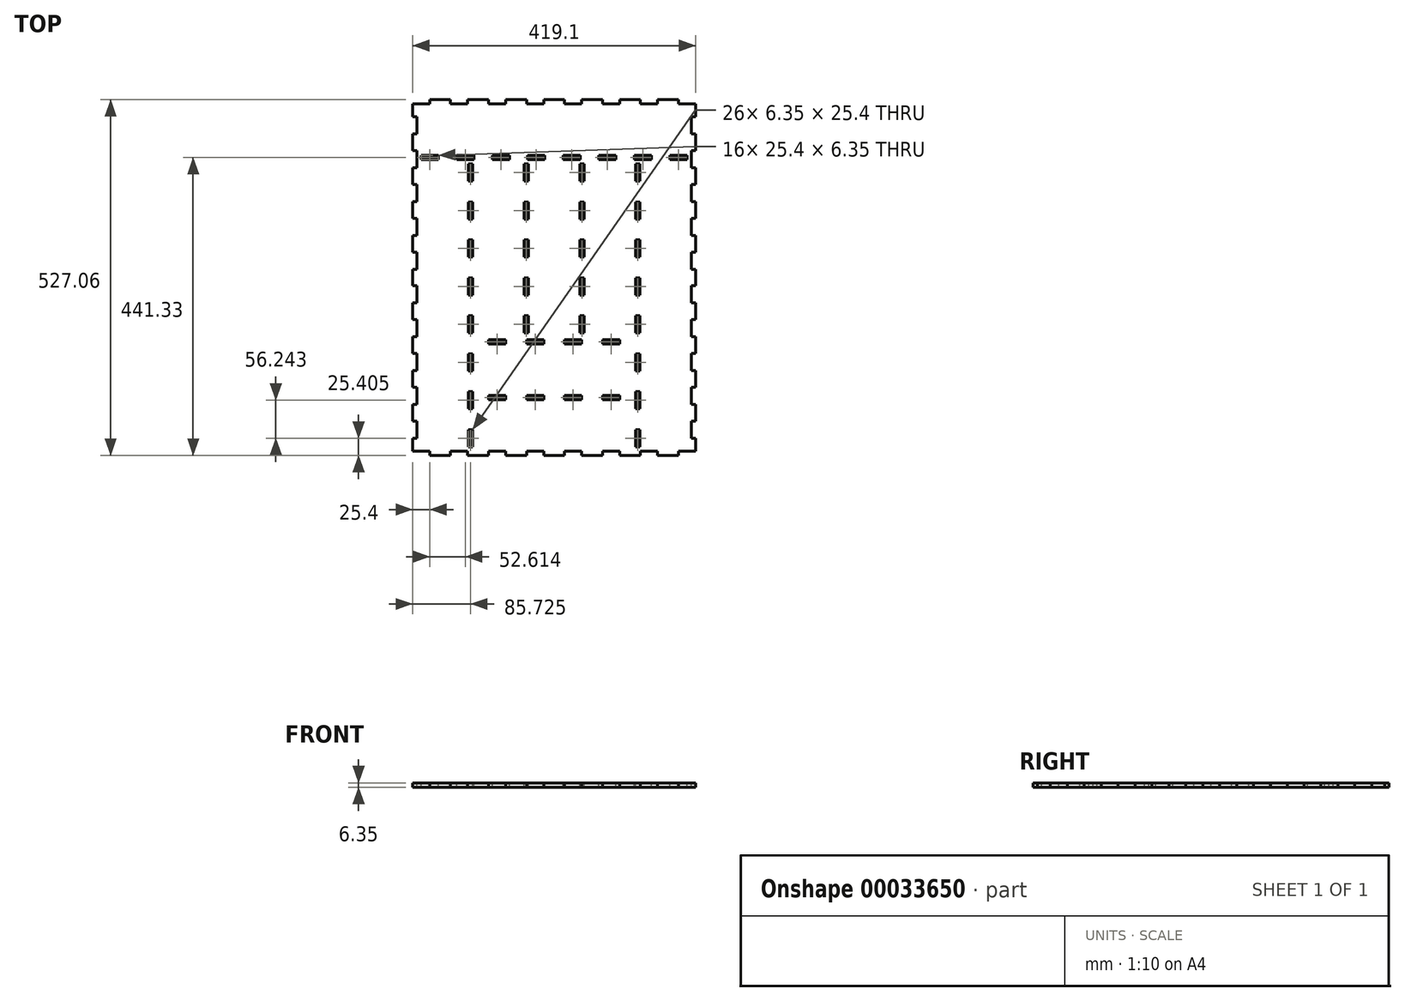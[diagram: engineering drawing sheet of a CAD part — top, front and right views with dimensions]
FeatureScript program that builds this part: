
annotation { "Feature Type Name" : "Feature", "Feature Type Description" : "" }
export const myFeature = defineFeature(function(context is Context, id is Id, definition is map)
    precondition{}
    {
        {
            var Q0;
            Q0=qCreatedBy(makeId("Top.planeOp"),FACE);
            var sketch = newSketch(context, id + "F0", { "sketchPlane" : qUnion([Q0])});
            skLineSegment(sketch, "E0.rect.bottom", {"start": v(209.55, 263.53) * mm, "end": v(-209.55, 263.53) * mm});
            skLineSegment(sketch, "E0.rect.top", {"start": v(209.55, -263.53) * mm, "end": v(-209.55, -263.53) * mm});
            skLineSegment(sketch, "E0.rect.left", {"start": v(209.55, 263.53) * mm, "end": v(209.55, -263.53) * mm});
            skLineSegment(sketch, "E0.rect.right", {"start": v(-209.55, 263.53) * mm, "end": v(-209.55, -263.53) * mm});
            skPoint(sketch, "E0.rect.middle", {"position": v(0, 0) * mm});
            skSolve(sketch);
        }
        {
            var Q0;
            Q0=makeQuery(id+"F0.imprint","IMPRINT",FACE,{"disambiguationData":[TD([[makeQuery(id+"F0.imprint","IMPRINT",EDGE,{"derivedFrom":sQuery(id+"F0.wireOp",EDGE,"E0.rect.bottom")}),1.0]])]});
            extrude(context, id + "F1", {"entities" : qUnion([Q0]), "depth" : 6.35 * mm});
        }
        {
            var Q0;
            Q0=makeQuery(id+"F1.opExtrude","CAP_FACE",FACE,{"disambiguationData":[OSD([sQuery(id+"F0.wireOp",EDGE,"E0.rect.bottom"),sQuery(id+"F0.wireOp",EDGE,"E0.rect.top"),sQuery(id+"F0.wireOp",EDGE,"E0.rect.left"),sQuery(id+"F0.wireOp",EDGE,"E0.rect.right")])],"isStart":false});
            var sketch = newSketch(context, id + "F2", { "sketchPlane" : qUnion([Q0])});
            skLineSegment(sketch, "E1.bottom", {"start": v(-209.55, -257.18) * mm, "end": v(-184.15, -257.18) * mm});
            skLineSegment(sketch, "E1.top", {"start": v(-209.55, -263.53) * mm, "end": v(-184.15, -263.53) * mm});
            skLineSegment(sketch, "E1.left", {"start": v(-209.55, -257.18) * mm, "end": v(-209.55, -263.53) * mm});
            skLineSegment(sketch, "E1.right", {"start": v(-184.15, -257.18) * mm, "end": v(-184.15, -263.53) * mm});
            skLineSegment(sketch, "E2", {"start": v(-209.55, 0) * mm, "end": v(209.55, 0) * mm, "construction": true});
            skLineSegment(sketch, "E3", {"start": v(0, 263.53) * mm, "end": v(0, -263.53) * mm, "construction": true});
            skLineSegment(sketch, "E4.1.0.0", {"start": v(-127.9, -257.18) * mm, "end": v(-127.9, -263.53) * mm});
            skLineSegment(sketch, "E4.1.0.1", {"start": v(-153.3, -257.18) * mm, "end": v(-153.3, -263.53) * mm});
            skLineSegment(sketch, "E4.1.0.2", {"start": v(-153.3, -263.53) * mm, "end": v(-127.9, -263.53) * mm});
            skLineSegment(sketch, "E4.1.0.3", {"start": v(-153.3, -257.18) * mm, "end": v(-127.9, -257.18) * mm});
            skLineSegment(sketch, "E4.2.0.0", {"start": v(-71.66, -257.18) * mm, "end": v(-71.66, -263.53) * mm});
            skLineSegment(sketch, "E4.2.0.1", {"start": v(-97.06, -257.18) * mm, "end": v(-97.06, -263.53) * mm});
            skLineSegment(sketch, "E4.2.0.2", {"start": v(-97.06, -263.53) * mm, "end": v(-71.66, -263.53) * mm});
            skLineSegment(sketch, "E4.2.0.3", {"start": v(-97.06, -257.18) * mm, "end": v(-71.66, -257.18) * mm});
            skLineSegment(sketch, "E4.3.0.0", {"start": v(-15.42, -257.18) * mm, "end": v(-15.42, -263.53) * mm});
            skLineSegment(sketch, "E4.3.0.1", {"start": v(-40.82, -257.18) * mm, "end": v(-40.82, -263.53) * mm});
            skLineSegment(sketch, "E4.3.0.2", {"start": v(-40.82, -263.53) * mm, "end": v(-15.42, -263.53) * mm});
            skLineSegment(sketch, "E4.3.0.3", {"start": v(-40.82, -257.18) * mm, "end": v(-15.42, -257.18) * mm});
            skLineSegment(sketch, "E4.4.0.0", {"start": v(40.82, -257.18) * mm, "end": v(40.82, -263.53) * mm});
            skLineSegment(sketch, "E4.4.0.1", {"start": v(15.42, -257.18) * mm, "end": v(15.42, -263.53) * mm});
            skLineSegment(sketch, "E4.4.0.2", {"start": v(15.42, -263.53) * mm, "end": v(40.82, -263.53) * mm});
            skLineSegment(sketch, "E4.4.0.3", {"start": v(15.42, -257.18) * mm, "end": v(40.82, -257.18) * mm});
            skLineSegment(sketch, "E4.5.0.0", {"start": v(97.06, -257.18) * mm, "end": v(97.06, -263.53) * mm});
            skLineSegment(sketch, "E4.5.0.1", {"start": v(71.66, -257.18) * mm, "end": v(71.66, -263.53) * mm});
            skLineSegment(sketch, "E4.5.0.2", {"start": v(71.66, -263.53) * mm, "end": v(97.06, -263.53) * mm});
            skLineSegment(sketch, "E4.5.0.3", {"start": v(71.66, -257.18) * mm, "end": v(97.06, -257.18) * mm});
            skLineSegment(sketch, "E4.6.0.0", {"start": v(153.3, -257.18) * mm, "end": v(153.3, -263.53) * mm});
            skLineSegment(sketch, "E4.6.0.1", {"start": v(127.9, -257.18) * mm, "end": v(127.9, -263.53) * mm});
            skLineSegment(sketch, "E4.6.0.2", {"start": v(127.9, -263.53) * mm, "end": v(153.3, -263.53) * mm});
            skLineSegment(sketch, "E4.6.0.3", {"start": v(127.9, -257.18) * mm, "end": v(153.3, -257.18) * mm});
            skLineSegment(sketch, "E4.7.0.0", {"start": v(209.55, -257.18) * mm, "end": v(209.55, -263.53) * mm});
            skLineSegment(sketch, "E4.7.0.1", {"start": v(184.15, -257.18) * mm, "end": v(184.15, -263.53) * mm});
            skLineSegment(sketch, "E4.7.0.2", {"start": v(184.15, -263.53) * mm, "end": v(209.55, -263.53) * mm});
            skLineSegment(sketch, "E4.7.0.3", {"start": v(184.15, -257.18) * mm, "end": v(209.55, -257.18) * mm});
            skLineSegment(sketch, "E4.direction1", {"start": v(-184.15, -263.53) * mm, "end": v(-127.9, -263.53) * mm, "construction": true});
            skLineSegment(sketch, "E5.MirrorCS", {"start": v(127.9, 257.18) * mm, "end": v(127.9, 263.53) * mm});
            skLineSegment(sketch, "E6.MirrorCS", {"start": v(15.42, 257.18) * mm, "end": v(15.42, 263.53) * mm});
            skLineSegment(sketch, "E7.MirrorCS", {"start": v(209.55, 257.18) * mm, "end": v(209.55, 263.53) * mm});
            skLineSegment(sketch, "E8.MirrorCS", {"start": v(184.15, 257.18) * mm, "end": v(184.15, 263.53) * mm});
            skLineSegment(sketch, "E9.MirrorCS", {"start": v(97.06, 257.18) * mm, "end": v(97.06, 263.53) * mm});
            skLineSegment(sketch, "E10.MirrorCS", {"start": v(71.66, 257.18) * mm, "end": v(71.66, 263.53) * mm});
            skLineSegment(sketch, "E11.MirrorCS", {"start": v(153.3, 257.18) * mm, "end": v(153.3, 263.53) * mm});
            skLineSegment(sketch, "E12.MirrorCS", {"start": v(40.82, 257.18) * mm, "end": v(40.82, 263.53) * mm});
            skLineSegment(sketch, "E13.MirrorCS", {"start": v(127.9, 257.18) * mm, "end": v(153.3, 257.18) * mm});
            skLineSegment(sketch, "E14.MirrorCS", {"start": v(15.42, 263.53) * mm, "end": v(40.82, 263.53) * mm});
            skLineSegment(sketch, "E15.MirrorCS", {"start": v(127.9, 263.53) * mm, "end": v(153.3, 263.53) * mm});
            skLineSegment(sketch, "E16.MirrorCS", {"start": v(15.42, 257.18) * mm, "end": v(40.82, 257.18) * mm});
            skLineSegment(sketch, "E17.MirrorCS", {"start": v(184.15, 263.53) * mm, "end": v(209.55, 263.53) * mm});
            skLineSegment(sketch, "E18.MirrorCS", {"start": v(71.66, 263.53) * mm, "end": v(97.06, 263.53) * mm});
            skLineSegment(sketch, "E19.MirrorCS", {"start": v(184.15, 257.18) * mm, "end": v(209.55, 257.18) * mm});
            skLineSegment(sketch, "E20.MirrorCS", {"start": v(71.66, 257.18) * mm, "end": v(97.06, 257.18) * mm});
            skLineSegment(sketch, "E21.MirrorCS", {"start": v(-127.9, 257.18) * mm, "end": v(-127.9, 263.53) * mm});
            skLineSegment(sketch, "E22.MirrorCS", {"start": v(-184.15, 257.18) * mm, "end": v(-184.15, 263.53) * mm});
            skLineSegment(sketch, "E23.MirrorCS", {"start": v(-153.3, 257.18) * mm, "end": v(-127.9, 257.18) * mm});
            skLineSegment(sketch, "E24.MirrorCS", {"start": v(-209.55, 263.53) * mm, "end": v(-184.15, 263.53) * mm});
            skLineSegment(sketch, "E25.MirrorCS", {"start": v(-40.82, 257.18) * mm, "end": v(-40.82, 263.53) * mm});
            skLineSegment(sketch, "E26.MirrorCS", {"start": v(-97.06, 263.53) * mm, "end": v(-71.66, 263.53) * mm});
            skLineSegment(sketch, "E27.MirrorCS", {"start": v(-97.06, 257.18) * mm, "end": v(-71.66, 257.18) * mm});
            skLineSegment(sketch, "E28.MirrorCS", {"start": v(-97.06, 257.18) * mm, "end": v(-97.06, 263.53) * mm});
            skLineSegment(sketch, "E29.MirrorCS", {"start": v(-71.66, 257.18) * mm, "end": v(-71.66, 263.53) * mm});
            skLineSegment(sketch, "E30.MirrorCS", {"start": v(-153.3, 263.53) * mm, "end": v(-127.9, 263.53) * mm});
            skLineSegment(sketch, "E31.MirrorCS", {"start": v(-153.3, 257.18) * mm, "end": v(-153.3, 263.53) * mm});
            skLineSegment(sketch, "E32.MirrorCS", {"start": v(-209.55, 257.18) * mm, "end": v(-209.55, 263.53) * mm});
            skLineSegment(sketch, "E33.MirrorCS", {"start": v(-209.55, 257.18) * mm, "end": v(-184.15, 257.18) * mm});
            skLineSegment(sketch, "E34.MirrorCS", {"start": v(-15.42, 257.18) * mm, "end": v(-15.42, 263.53) * mm});
            skLineSegment(sketch, "E35.MirrorCS", {"start": v(-184.15, 263.53) * mm, "end": v(-127.9, 263.53) * mm});
            skLineSegment(sketch, "E36.MirrorCS", {"start": v(-40.82, 257.18) * mm, "end": v(-15.42, 257.18) * mm});
            skLineSegment(sketch, "E37.MirrorCS", {"start": v(-40.82, 263.53) * mm, "end": v(-15.42, 263.53) * mm});
            skLineSegment(sketch, "E38.bottom", {"start": v(-209.55, 238.13) * mm, "end": v(-203.2, 238.13) * mm});
            skLineSegment(sketch, "E38.top", {"start": v(-209.55, 212.73) * mm, "end": v(-203.2, 212.73) * mm});
            skLineSegment(sketch, "E38.left", {"start": v(-209.55, 238.13) * mm, "end": v(-209.55, 212.73) * mm});
            skLineSegment(sketch, "E38.right", {"start": v(-203.2, 238.13) * mm, "end": v(-203.2, 212.73) * mm});
            skLineSegment(sketch, "E39.1.0.0", {"start": v(-209.55, 188.03) * mm, "end": v(-209.55, 162.63) * mm});
            skLineSegment(sketch, "E39.1.0.1", {"start": v(-203.2, 188.03) * mm, "end": v(-203.2, 162.63) * mm});
            skLineSegment(sketch, "E39.1.0.2", {"start": v(-209.55, 162.63) * mm, "end": v(-203.2, 162.63) * mm});
            skLineSegment(sketch, "E39.1.0.3", {"start": v(-209.55, 188.03) * mm, "end": v(-203.2, 188.03) * mm});
            skLineSegment(sketch, "E39.2.0.0", {"start": v(-209.55, 137.94) * mm, "end": v(-209.55, 112.54) * mm});
            skLineSegment(sketch, "E39.2.0.1", {"start": v(-203.2, 137.94) * mm, "end": v(-203.2, 112.54) * mm});
            skLineSegment(sketch, "E39.2.0.2", {"start": v(-209.55, 112.54) * mm, "end": v(-203.2, 112.54) * mm});
            skLineSegment(sketch, "E39.2.0.3", {"start": v(-209.55, 137.94) * mm, "end": v(-203.2, 137.94) * mm});
            skLineSegment(sketch, "E39.3.0.0", {"start": v(-209.55, 87.84) * mm, "end": v(-209.55, 62.44) * mm});
            skLineSegment(sketch, "E39.3.0.1", {"start": v(-203.2, 87.84) * mm, "end": v(-203.2, 62.44) * mm});
            skLineSegment(sketch, "E39.3.0.2", {"start": v(-209.55, 62.44) * mm, "end": v(-203.2, 62.44) * mm});
            skLineSegment(sketch, "E39.3.0.3", {"start": v(-209.55, 87.84) * mm, "end": v(-203.2, 87.84) * mm});
            skLineSegment(sketch, "E39.4.0.0", {"start": v(-209.55, 37.75) * mm, "end": v(-209.55, 12.35) * mm});
            skLineSegment(sketch, "E39.4.0.1", {"start": v(-203.2, 37.75) * mm, "end": v(-203.2, 12.35) * mm});
            skLineSegment(sketch, "E39.4.0.2", {"start": v(-209.55, 12.35) * mm, "end": v(-203.2, 12.35) * mm});
            skLineSegment(sketch, "E39.4.0.3", {"start": v(-209.55, 37.75) * mm, "end": v(-203.2, 37.75) * mm});
            skLineSegment(sketch, "E39.5.0.0", {"start": v(-209.55, -12.35) * mm, "end": v(-209.55, -37.75) * mm});
            skLineSegment(sketch, "E39.5.0.1", {"start": v(-203.2, -12.35) * mm, "end": v(-203.2, -37.75) * mm});
            skLineSegment(sketch, "E39.5.0.2", {"start": v(-209.55, -37.75) * mm, "end": v(-203.2, -37.75) * mm});
            skLineSegment(sketch, "E39.5.0.3", {"start": v(-209.55, -12.35) * mm, "end": v(-203.2, -12.35) * mm});
            skLineSegment(sketch, "E39.6.0.0", {"start": v(-209.55, -62.44) * mm, "end": v(-209.55, -87.84) * mm});
            skLineSegment(sketch, "E39.6.0.1", {"start": v(-203.2, -62.44) * mm, "end": v(-203.2, -87.84) * mm});
            skLineSegment(sketch, "E39.6.0.2", {"start": v(-209.55, -87.84) * mm, "end": v(-203.2, -87.84) * mm});
            skLineSegment(sketch, "E39.6.0.3", {"start": v(-209.55, -62.44) * mm, "end": v(-203.2, -62.44) * mm});
            skLineSegment(sketch, "E39.7.0.0", {"start": v(-209.55, -112.54) * mm, "end": v(-209.55, -137.94) * mm});
            skLineSegment(sketch, "E39.7.0.1", {"start": v(-203.2, -112.54) * mm, "end": v(-203.2, -137.94) * mm});
            skLineSegment(sketch, "E39.7.0.2", {"start": v(-209.55, -137.94) * mm, "end": v(-203.2, -137.94) * mm});
            skLineSegment(sketch, "E39.7.0.3", {"start": v(-209.55, -112.54) * mm, "end": v(-203.2, -112.54) * mm});
            skLineSegment(sketch, "E39.8.0.0", {"start": v(-209.55, -162.63) * mm, "end": v(-209.55, -188.03) * mm});
            skLineSegment(sketch, "E39.8.0.1", {"start": v(-203.2, -162.63) * mm, "end": v(-203.2, -188.03) * mm});
            skLineSegment(sketch, "E39.8.0.2", {"start": v(-209.55, -188.03) * mm, "end": v(-203.2, -188.03) * mm});
            skLineSegment(sketch, "E39.8.0.3", {"start": v(-209.55, -162.63) * mm, "end": v(-203.2, -162.63) * mm});
            skLineSegment(sketch, "E39.9.0.0", {"start": v(-209.55, -212.73) * mm, "end": v(-209.55, -238.12) * mm});
            skLineSegment(sketch, "E39.9.0.1", {"start": v(-203.2, -212.73) * mm, "end": v(-203.2, -238.13) * mm});
            skLineSegment(sketch, "E39.9.0.2", {"start": v(-209.55, -238.12) * mm, "end": v(-203.2, -238.12) * mm});
            skLineSegment(sketch, "E39.9.0.3", {"start": v(-209.55, -212.73) * mm, "end": v(-203.2, -212.73) * mm});
            skLineSegment(sketch, "E39.direction1", {"start": v(-209.55, 212.73) * mm, "end": v(-209.55, 162.63) * mm, "construction": true});
            skLineSegment(sketch, "E40.MirrorCS", {"start": v(209.55, 162.63) * mm, "end": v(203.2, 162.63) * mm});
            skLineSegment(sketch, "E41.MirrorCS", {"start": v(209.55, 212.73) * mm, "end": v(203.2, 212.73) * mm});
            skLineSegment(sketch, "E42.MirrorCS", {"start": v(209.55, 87.84) * mm, "end": v(203.2, 87.84) * mm});
            skLineSegment(sketch, "E43.MirrorCS", {"start": v(209.55, -112.54) * mm, "end": v(203.2, -112.54) * mm});
            skLineSegment(sketch, "E44.MirrorCS", {"start": v(209.55, -37.75) * mm, "end": v(203.2, -37.75) * mm});
            skLineSegment(sketch, "E45.MirrorCS", {"start": v(209.55, -238.12) * mm, "end": v(203.2, -238.12) * mm});
            skLineSegment(sketch, "E46.MirrorCS", {"start": v(209.55, 62.44) * mm, "end": v(203.2, 62.44) * mm});
            skLineSegment(sketch, "E47.MirrorCS", {"start": v(209.55, -137.94) * mm, "end": v(203.2, -137.94) * mm});
            skLineSegment(sketch, "E48.MirrorCS", {"start": v(209.55, 188.03) * mm, "end": v(203.2, 188.03) * mm});
            skLineSegment(sketch, "E49.MirrorCS", {"start": v(209.55, -12.35) * mm, "end": v(203.2, -12.35) * mm});
            skLineSegment(sketch, "E50.MirrorCS", {"start": v(209.55, -212.72) * mm, "end": v(203.2, -212.72) * mm});
            skLineSegment(sketch, "E51.MirrorCS", {"start": v(209.55, 12.35) * mm, "end": v(203.2, 12.35) * mm});
            skLineSegment(sketch, "E52.MirrorCS", {"start": v(209.55, 137.94) * mm, "end": v(203.2, 137.94) * mm});
            skLineSegment(sketch, "E53.MirrorCS", {"start": v(209.55, -87.84) * mm, "end": v(203.2, -87.84) * mm});
            skLineSegment(sketch, "E54.MirrorCS", {"start": v(209.55, 238.13) * mm, "end": v(203.2, 238.13) * mm});
            skLineSegment(sketch, "E55.MirrorCS", {"start": v(209.55, 112.54) * mm, "end": v(203.2, 112.54) * mm});
            skLineSegment(sketch, "E56.MirrorCS", {"start": v(209.55, -62.44) * mm, "end": v(203.2, -62.44) * mm});
            skLineSegment(sketch, "E57.MirrorCS", {"start": v(209.55, -188.03) * mm, "end": v(203.2, -188.03) * mm});
            skLineSegment(sketch, "E58.MirrorCS", {"start": v(209.55, 37.75) * mm, "end": v(203.2, 37.75) * mm});
            skLineSegment(sketch, "E59.MirrorCS", {"start": v(209.55, -162.63) * mm, "end": v(203.2, -162.63) * mm});
            skLineSegment(sketch, "E60.MirrorCS", {"start": v(203.2, -12.35) * mm, "end": v(203.2, -37.75) * mm});
            skLineSegment(sketch, "E61.MirrorCS", {"start": v(203.2, -212.72) * mm, "end": v(203.2, -238.12) * mm});
            skLineSegment(sketch, "E62.MirrorCS", {"start": v(203.2, 188.03) * mm, "end": v(203.2, 162.63) * mm});
            skLineSegment(sketch, "E63.MirrorCS", {"start": v(203.2, -162.63) * mm, "end": v(203.2, -188.03) * mm});
            skLineSegment(sketch, "E64.MirrorCS", {"start": v(209.55, -112.54) * mm, "end": v(209.55, -137.94) * mm});
            skLineSegment(sketch, "E65.MirrorCS", {"start": v(209.55, -212.72) * mm, "end": v(209.55, -238.12) * mm});
            skLineSegment(sketch, "E66.MirrorCS", {"start": v(209.55, 87.84) * mm, "end": v(209.55, 62.44) * mm});
            skLineSegment(sketch, "E67.MirrorCS", {"start": v(209.55, 212.73) * mm, "end": v(209.55, 162.63) * mm});
            skLineSegment(sketch, "E68.MirrorCS", {"start": v(209.55, 137.94) * mm, "end": v(209.55, 112.54) * mm});
            skLineSegment(sketch, "E69.MirrorCS", {"start": v(203.2, 238.13) * mm, "end": v(203.2, 212.73) * mm});
            skLineSegment(sketch, "E70.MirrorCS", {"start": v(209.55, -62.44) * mm, "end": v(209.55, -87.84) * mm});
            skLineSegment(sketch, "E71.MirrorCS", {"start": v(203.2, 37.75) * mm, "end": v(203.2, 12.35) * mm});
            skLineSegment(sketch, "E72.MirrorCS", {"start": v(203.2, 137.94) * mm, "end": v(203.2, 112.54) * mm});
            skLineSegment(sketch, "E73.MirrorCS", {"start": v(209.55, 37.75) * mm, "end": v(209.55, 12.35) * mm});
            skLineSegment(sketch, "E74.MirrorCS", {"start": v(203.2, -62.44) * mm, "end": v(203.2, -87.84) * mm});
            skLineSegment(sketch, "E75.MirrorCS", {"start": v(209.55, -162.63) * mm, "end": v(209.55, -188.03) * mm});
            skLineSegment(sketch, "E76.MirrorCS", {"start": v(209.55, -12.35) * mm, "end": v(209.55, -37.75) * mm});
            skLineSegment(sketch, "E77.MirrorCS", {"start": v(203.2, -112.54) * mm, "end": v(203.2, -137.94) * mm});
            skLineSegment(sketch, "E78.MirrorCS", {"start": v(209.55, 188.03) * mm, "end": v(209.55, 162.63) * mm});
            skLineSegment(sketch, "E79.MirrorCS", {"start": v(203.2, 87.84) * mm, "end": v(203.2, 62.44) * mm});
            skLineSegment(sketch, "E80.MirrorCS", {"start": v(209.55, 238.13) * mm, "end": v(209.55, 212.73) * mm});
            skSolve(sketch);
        }
        {
            var Q0;
            Q0 = qSketchRegion(id + "F2", true);
            extrude(context, id + "F3", {"entities" : qUnion([Q0]), "operationType" : NewBodyOperationType.REMOVE, "endBound" : BoundingType.THROUGH_ALL, "oppositeDirection" : true, "depth" : 25.4 * mm});
        }
        {
            var Q0;
            Q0=makeQuery(id+"F1.opExtrude","CAP_FACE",FACE,{"disambiguationData":[OSD([sQuery(id+"F0.wireOp",EDGE,"E0.rect.bottom"),sQuery(id+"F0.wireOp",EDGE,"E0.rect.top"),sQuery(id+"F0.wireOp",EDGE,"E0.rect.left"),sQuery(id+"F0.wireOp",EDGE,"E0.rect.right")])],"isStart":false});
            var sketch = newSketch(context, id + "F4", { "sketchPlane" : qUnion([Q0])});
            skLineSegment(sketch, "E81.bottom", {"start": v(-196.85, 180.98) * mm, "end": v(-171.45, 180.98) * mm});
            skLineSegment(sketch, "E81.top", {"start": v(-196.85, 174.63) * mm, "end": v(-171.45, 174.63) * mm});
            skLineSegment(sketch, "E81.left", {"start": v(-196.85, 180.98) * mm, "end": v(-196.85, 174.63) * mm});
            skLineSegment(sketch, "E81.right", {"start": v(-171.45, 180.98) * mm, "end": v(-171.45, 174.63) * mm});
            skLineSegment(sketch, "E82.1.0.0", {"start": v(-144.24, 180.98) * mm, "end": v(-118.84, 180.98) * mm});
            skLineSegment(sketch, "E82.1.0.1", {"start": v(-144.24, 174.63) * mm, "end": v(-118.84, 174.63) * mm});
            skLineSegment(sketch, "E82.1.0.2", {"start": v(-144.24, 180.98) * mm, "end": v(-144.24, 174.63) * mm});
            skLineSegment(sketch, "E82.1.0.3", {"start": v(-118.84, 180.98) * mm, "end": v(-118.84, 174.63) * mm});
            skLineSegment(sketch, "E82.2.0.0", {"start": v(-91.62, 180.98) * mm, "end": v(-66.22, 180.98) * mm});
            skLineSegment(sketch, "E82.2.0.1", {"start": v(-91.62, 174.63) * mm, "end": v(-66.22, 174.63) * mm});
            skLineSegment(sketch, "E82.2.0.2", {"start": v(-91.62, 180.98) * mm, "end": v(-91.62, 174.63) * mm});
            skLineSegment(sketch, "E82.2.0.3", {"start": v(-66.22, 180.98) * mm, "end": v(-66.22, 174.63) * mm});
            skLineSegment(sketch, "E82.3.0.0", {"start": v(-39, 180.98) * mm, "end": v(-13.6, 180.98) * mm});
            skLineSegment(sketch, "E82.3.0.1", {"start": v(-39, 174.63) * mm, "end": v(-13.6, 174.63) * mm});
            skLineSegment(sketch, "E82.3.0.2", {"start": v(-39, 180.98) * mm, "end": v(-39, 174.63) * mm});
            skLineSegment(sketch, "E82.3.0.3", {"start": v(-13.6, 180.98) * mm, "end": v(-13.6, 174.63) * mm});
            skLineSegment(sketch, "E82.4.0.0", {"start": v(13.6, 180.98) * mm, "end": v(39, 180.98) * mm});
            skLineSegment(sketch, "E82.4.0.1", {"start": v(13.6, 174.63) * mm, "end": v(39, 174.63) * mm});
            skLineSegment(sketch, "E82.4.0.2", {"start": v(13.6, 180.98) * mm, "end": v(13.6, 174.63) * mm});
            skLineSegment(sketch, "E82.4.0.3", {"start": v(39, 180.98) * mm, "end": v(39, 174.63) * mm});
            skLineSegment(sketch, "E82.5.0.0", {"start": v(66.22, 180.98) * mm, "end": v(91.62, 180.98) * mm});
            skLineSegment(sketch, "E82.5.0.1", {"start": v(66.22, 174.63) * mm, "end": v(91.62, 174.63) * mm});
            skLineSegment(sketch, "E82.5.0.2", {"start": v(66.22, 180.98) * mm, "end": v(66.22, 174.63) * mm});
            skLineSegment(sketch, "E82.5.0.3", {"start": v(91.62, 180.98) * mm, "end": v(91.62, 174.63) * mm});
            skLineSegment(sketch, "E82.6.0.0", {"start": v(118.84, 180.98) * mm, "end": v(144.24, 180.98) * mm});
            skLineSegment(sketch, "E82.6.0.1", {"start": v(118.84, 174.63) * mm, "end": v(144.24, 174.63) * mm});
            skLineSegment(sketch, "E82.6.0.2", {"start": v(118.84, 180.98) * mm, "end": v(118.84, 174.63) * mm});
            skLineSegment(sketch, "E82.6.0.3", {"start": v(144.24, 180.98) * mm, "end": v(144.24, 174.63) * mm});
            skLineSegment(sketch, "E82.7.0.0", {"start": v(171.45, 180.98) * mm, "end": v(196.85, 180.98) * mm});
            skLineSegment(sketch, "E82.7.0.1", {"start": v(171.45, 174.63) * mm, "end": v(196.85, 174.63) * mm});
            skLineSegment(sketch, "E82.7.0.2", {"start": v(171.45, 180.98) * mm, "end": v(171.45, 174.63) * mm});
            skLineSegment(sketch, "E82.7.0.3", {"start": v(196.85, 180.98) * mm, "end": v(196.85, 174.63) * mm});
            skLineSegment(sketch, "E82.direction1", {"start": v(-196.85, 180.98) * mm, "end": v(-144.24, 180.98) * mm, "construction": true});
            skSolve(sketch);
        }
        {
            var Q0;
            Q0 = qSketchRegion(id + "F4", true);
            extrude(context, id + "F5", {"entities" : qUnion([Q0]), "operationType" : NewBodyOperationType.REMOVE, "endBound" : BoundingType.THROUGH_ALL, "oppositeDirection" : true, "depth" : 25.4 * mm});
        }
        {
            var Q0;
            Q0=makeQuery(id+"F1.opExtrude","CAP_FACE",FACE,{"disambiguationData":[OSD([sQuery(id+"F0.wireOp",EDGE,"E0.rect.bottom"),sQuery(id+"F0.wireOp",EDGE,"E0.rect.top"),sQuery(id+"F0.wireOp",EDGE,"E0.rect.left"),sQuery(id+"F0.wireOp",EDGE,"E0.rect.right")])],"isStart":false});
            var sketch = newSketch(context, id + "F6", { "sketchPlane" : qUnion([Q0])});
            skLineSegment(sketch, "E83.bottom", {"start": v(-127, -250.82) * mm, "end": v(-120.65, -250.82) * mm});
            skLineSegment(sketch, "E83.top", {"start": v(-127, -225.42) * mm, "end": v(-120.65, -225.42) * mm});
            skLineSegment(sketch, "E83.left", {"start": v(-127, -250.82) * mm, "end": v(-127, -225.42) * mm});
            skLineSegment(sketch, "E83.right", {"start": v(-120.65, -250.82) * mm, "end": v(-120.65, -225.42) * mm});
            skLineSegment(sketch, "E84.0.1.0", {"start": v(-120.65, -194.58) * mm, "end": v(-120.65, -169.18) * mm});
            skLineSegment(sketch, "E84.0.1.1", {"start": v(-127, -194.58) * mm, "end": v(-127, -169.18) * mm});
            skLineSegment(sketch, "E84.0.1.2", {"start": v(-127, -169.18) * mm, "end": v(-120.65, -169.18) * mm});
            skLineSegment(sketch, "E84.0.1.3", {"start": v(-127, -194.58) * mm, "end": v(-120.65, -194.58) * mm});
            skLineSegment(sketch, "E84.0.2.0", {"start": v(-120.65, -138.34) * mm, "end": v(-120.65, -112.94) * mm});
            skLineSegment(sketch, "E84.0.2.1", {"start": v(-127, -138.34) * mm, "end": v(-127, -112.94) * mm});
            skLineSegment(sketch, "E84.0.2.2", {"start": v(-127, -112.94) * mm, "end": v(-120.65, -112.94) * mm});
            skLineSegment(sketch, "E84.0.2.3", {"start": v(-127, -138.34) * mm, "end": v(-120.65, -138.34) * mm});
            skLineSegment(sketch, "E84.0.3.0", {"start": v(-120.65, -82.1) * mm, "end": v(-120.65, -56.7) * mm});
            skLineSegment(sketch, "E84.0.3.1", {"start": v(-127, -82.1) * mm, "end": v(-127, -56.7) * mm});
            skLineSegment(sketch, "E84.0.3.2", {"start": v(-127, -56.7) * mm, "end": v(-120.65, -56.7) * mm});
            skLineSegment(sketch, "E84.0.3.3", {"start": v(-127, -82.1) * mm, "end": v(-120.65, -82.1) * mm});
            skLineSegment(sketch, "E84.0.4.0", {"start": v(-120.65, -25.85) * mm, "end": v(-120.65, -0.45) * mm});
            skLineSegment(sketch, "E84.0.4.1", {"start": v(-127, -25.85) * mm, "end": v(-127, -0.45) * mm});
            skLineSegment(sketch, "E84.0.4.2", {"start": v(-127, -0.45) * mm, "end": v(-120.65, -0.45) * mm});
            skLineSegment(sketch, "E84.0.4.3", {"start": v(-127, -25.85) * mm, "end": v(-120.65, -25.85) * mm});
            skLineSegment(sketch, "E84.0.5.0", {"start": v(-120.65, 30.39) * mm, "end": v(-120.65, 55.79) * mm});
            skLineSegment(sketch, "E84.0.5.1", {"start": v(-127, 30.39) * mm, "end": v(-127, 55.79) * mm});
            skLineSegment(sketch, "E84.0.5.2", {"start": v(-127, 55.79) * mm, "end": v(-120.65, 55.79) * mm});
            skLineSegment(sketch, "E84.0.5.3", {"start": v(-127, 30.39) * mm, "end": v(-120.65, 30.39) * mm});
            skLineSegment(sketch, "E84.0.6.0", {"start": v(-120.65, 86.63) * mm, "end": v(-120.65, 112.03) * mm});
            skLineSegment(sketch, "E84.0.6.1", {"start": v(-127, 86.63) * mm, "end": v(-127, 112.03) * mm});
            skLineSegment(sketch, "E84.0.6.2", {"start": v(-127, 112.03) * mm, "end": v(-120.65, 112.03) * mm});
            skLineSegment(sketch, "E84.0.6.3", {"start": v(-127, 86.63) * mm, "end": v(-120.65, 86.63) * mm});
            skLineSegment(sketch, "E84.0.7.0", {"start": v(-120.65, 142.88) * mm, "end": v(-120.65, 168.28) * mm});
            skLineSegment(sketch, "E84.0.7.1", {"start": v(-127, 142.88) * mm, "end": v(-127, 168.28) * mm});
            skLineSegment(sketch, "E84.0.7.2", {"start": v(-127, 168.28) * mm, "end": v(-120.65, 168.28) * mm});
            skLineSegment(sketch, "E84.0.7.3", {"start": v(-127, 142.88) * mm, "end": v(-120.65, 142.88) * mm});
            skLineSegment(sketch, "E84.direction1", {"start": v(-120.65, -250.82) * mm, "end": v(-97.06, -250.82) * mm, "construction": true});
            skLineSegment(sketch, "E84.direction2", {"start": v(-120.65, -250.82) * mm, "end": v(-120.65, -194.58) * mm, "construction": true});
            skLineSegment(sketch, "E85", {"start": v(0, 263.53) * mm, "end": v(0, -263.53) * mm, "construction": true});
            skLineSegment(sketch, "E86.MirrorCS", {"start": v(127, -250.82) * mm, "end": v(120.65, -250.82) * mm});
            skLineSegment(sketch, "E87.MirrorCS", {"start": v(127, -112.94) * mm, "end": v(120.65, -112.94) * mm});
            skLineSegment(sketch, "E88.MirrorCS", {"start": v(127, 30.39) * mm, "end": v(120.65, 30.39) * mm});
            skLineSegment(sketch, "E89.MirrorCS", {"start": v(127, -0.45) * mm, "end": v(120.65, -0.45) * mm});
            skLineSegment(sketch, "E90.MirrorCS", {"start": v(127, 112.03) * mm, "end": v(120.65, 112.03) * mm});
            skLineSegment(sketch, "E91.MirrorCS", {"start": v(127, 142.88) * mm, "end": v(120.65, 142.88) * mm});
            skLineSegment(sketch, "E92.MirrorCS", {"start": v(127, -82.1) * mm, "end": v(120.65, -82.1) * mm});
            skLineSegment(sketch, "E93.MirrorCS", {"start": v(127, -225.42) * mm, "end": v(120.65, -225.42) * mm});
            skLineSegment(sketch, "E94.MirrorCS", {"start": v(127, -194.58) * mm, "end": v(120.65, -194.58) * mm});
            skLineSegment(sketch, "E95.MirrorCS", {"start": v(127, -169.18) * mm, "end": v(120.65, -169.18) * mm});
            skLineSegment(sketch, "E96.MirrorCS", {"start": v(127, -138.34) * mm, "end": v(120.65, -138.34) * mm});
            skLineSegment(sketch, "E97.MirrorCS", {"start": v(127, -25.85) * mm, "end": v(120.65, -25.85) * mm});
            skLineSegment(sketch, "E98.MirrorCS", {"start": v(127, 86.63) * mm, "end": v(120.65, 86.63) * mm});
            skLineSegment(sketch, "E99.MirrorCS", {"start": v(127, 168.28) * mm, "end": v(120.65, 168.28) * mm});
            skLineSegment(sketch, "E100.MirrorCS", {"start": v(127, 55.79) * mm, "end": v(120.65, 55.79) * mm});
            skLineSegment(sketch, "E101.MirrorCS", {"start": v(127, -56.7) * mm, "end": v(120.65, -56.7) * mm});
            skLineSegment(sketch, "E102.MirrorCS", {"start": v(120.65, -138.34) * mm, "end": v(120.65, -112.94) * mm});
            skLineSegment(sketch, "E103.MirrorCS", {"start": v(127, -138.34) * mm, "end": v(127, -112.94) * mm});
            skLineSegment(sketch, "E104.MirrorCS", {"start": v(120.65, -25.85) * mm, "end": v(120.65, -0.45) * mm});
            skLineSegment(sketch, "E105.MirrorCS", {"start": v(120.65, -82.1) * mm, "end": v(120.65, -56.7) * mm});
            skLineSegment(sketch, "E106.MirrorCS", {"start": v(127, -25.85) * mm, "end": v(127, -0.45) * mm});
            skLineSegment(sketch, "E107.MirrorCS", {"start": v(120.65, 86.63) * mm, "end": v(120.65, 112.03) * mm});
            skLineSegment(sketch, "E108.MirrorCS", {"start": v(127, 86.63) * mm, "end": v(127, 112.03) * mm});
            skLineSegment(sketch, "E109.MirrorCS", {"start": v(127, 142.88) * mm, "end": v(127, 168.28) * mm});
            skLineSegment(sketch, "E110.MirrorCS", {"start": v(120.65, 30.39) * mm, "end": v(120.65, 55.79) * mm});
            skLineSegment(sketch, "E111.MirrorCS", {"start": v(120.65, 142.88) * mm, "end": v(120.65, 168.28) * mm});
            skLineSegment(sketch, "E112.MirrorCS", {"start": v(127, 30.39) * mm, "end": v(127, 55.79) * mm});
            skLineSegment(sketch, "E113.MirrorCS", {"start": v(127, -82.1) * mm, "end": v(127, -56.7) * mm});
            skLineSegment(sketch, "E114.MirrorCS", {"start": v(127, -250.82) * mm, "end": v(127, -225.42) * mm});
            skLineSegment(sketch, "E115.MirrorCS", {"start": v(120.65, -250.82) * mm, "end": v(120.65, -225.42) * mm});
            skLineSegment(sketch, "E116.MirrorCS", {"start": v(120.65, -194.58) * mm, "end": v(120.65, -169.18) * mm});
            skLineSegment(sketch, "E117.MirrorCS", {"start": v(127, -194.58) * mm, "end": v(127, -169.18) * mm});
            skLineSegment(sketch, "E118.1.0.0", {"start": v(-38.1, -25.85) * mm, "end": v(-38.1, -0.45) * mm});
            skLineSegment(sketch, "E118.1.0.1", {"start": v(-38.1, -82.1) * mm, "end": v(-38.1, -56.7) * mm});
            skLineSegment(sketch, "E118.1.0.2", {"start": v(-44.45, -25.85) * mm, "end": v(-44.45, -0.45) * mm});
            skLineSegment(sketch, "E118.1.0.3", {"start": v(-38.1, 30.39) * mm, "end": v(-38.1, 55.79) * mm});
            skLineSegment(sketch, "E118.1.0.4", {"start": v(-44.45, 30.39) * mm, "end": v(-44.45, 55.79) * mm});
            skLineSegment(sketch, "E118.1.0.5", {"start": v(-38.1, 86.63) * mm, "end": v(-38.1, 112.03) * mm});
            skLineSegment(sketch, "E118.1.0.6", {"start": v(-44.45, 86.63) * mm, "end": v(-44.45, 112.03) * mm});
            skLineSegment(sketch, "E118.1.0.7", {"start": v(-44.45, 142.88) * mm, "end": v(-44.45, 168.28) * mm});
            skLineSegment(sketch, "E118.1.0.8", {"start": v(-38.1, 142.88) * mm, "end": v(-38.1, 168.28) * mm});
            skLineSegment(sketch, "E118.1.0.9", {"start": v(-44.45, -82.1) * mm, "end": v(-44.45, -56.7) * mm});
            skLineSegment(sketch, "E118.1.0.10", {"start": v(-44.45, -25.85) * mm, "end": v(-38.1, -25.85) * mm});
            skLineSegment(sketch, "E118.1.0.11", {"start": v(-44.45, -0.45) * mm, "end": v(-38.1, -0.45) * mm});
            skLineSegment(sketch, "E118.1.0.12", {"start": v(-44.45, 55.79) * mm, "end": v(-38.1, 55.79) * mm});
            skLineSegment(sketch, "E118.1.0.13", {"start": v(-44.45, 30.39) * mm, "end": v(-38.1, 30.39) * mm});
            skLineSegment(sketch, "E118.1.0.14", {"start": v(-44.45, 112.03) * mm, "end": v(-38.1, 112.03) * mm});
            skLineSegment(sketch, "E118.1.0.15", {"start": v(-44.45, 86.63) * mm, "end": v(-38.1, 86.63) * mm});
            skLineSegment(sketch, "E118.1.0.16", {"start": v(-44.45, 168.28) * mm, "end": v(-38.1, 168.28) * mm});
            skLineSegment(sketch, "E118.1.0.17", {"start": v(-44.45, 142.88) * mm, "end": v(-38.1, 142.88) * mm});
            skLineSegment(sketch, "E118.1.0.18", {"start": v(-44.45, -56.7) * mm, "end": v(-38.1, -56.7) * mm});
            skLineSegment(sketch, "E118.1.0.19", {"start": v(-44.45, -82.1) * mm, "end": v(-38.1, -82.1) * mm});
            skLineSegment(sketch, "E118.2.0.0", {"start": v(44.45, -25.85) * mm, "end": v(44.45, -0.45) * mm});
            skLineSegment(sketch, "E118.2.0.1", {"start": v(44.45, -82.1) * mm, "end": v(44.45, -56.7) * mm});
            skLineSegment(sketch, "E118.2.0.2", {"start": v(38.1, -25.85) * mm, "end": v(38.1, -0.45) * mm});
            skLineSegment(sketch, "E118.2.0.3", {"start": v(44.45, 30.39) * mm, "end": v(44.45, 55.79) * mm});
            skLineSegment(sketch, "E118.2.0.4", {"start": v(38.1, 30.39) * mm, "end": v(38.1, 55.79) * mm});
            skLineSegment(sketch, "E118.2.0.5", {"start": v(44.45, 86.63) * mm, "end": v(44.45, 112.03) * mm});
            skLineSegment(sketch, "E118.2.0.6", {"start": v(38.1, 86.63) * mm, "end": v(38.1, 112.03) * mm});
            skLineSegment(sketch, "E118.2.0.7", {"start": v(38.1, 142.88) * mm, "end": v(38.1, 168.28) * mm});
            skLineSegment(sketch, "E118.2.0.8", {"start": v(44.45, 142.88) * mm, "end": v(44.45, 168.28) * mm});
            skLineSegment(sketch, "E118.2.0.9", {"start": v(38.1, -82.1) * mm, "end": v(38.1, -56.7) * mm});
            skLineSegment(sketch, "E118.2.0.10", {"start": v(38.1, -25.85) * mm, "end": v(44.45, -25.85) * mm});
            skLineSegment(sketch, "E118.2.0.11", {"start": v(38.1, -0.45) * mm, "end": v(44.45, -0.45) * mm});
            skLineSegment(sketch, "E118.2.0.12", {"start": v(38.1, 55.79) * mm, "end": v(44.45, 55.79) * mm});
            skLineSegment(sketch, "E118.2.0.13", {"start": v(38.1, 30.39) * mm, "end": v(44.45, 30.39) * mm});
            skLineSegment(sketch, "E118.2.0.14", {"start": v(38.1, 112.03) * mm, "end": v(44.45, 112.03) * mm});
            skLineSegment(sketch, "E118.2.0.15", {"start": v(38.1, 86.63) * mm, "end": v(44.45, 86.63) * mm});
            skLineSegment(sketch, "E118.2.0.16", {"start": v(38.1, 168.28) * mm, "end": v(44.45, 168.28) * mm});
            skLineSegment(sketch, "E118.2.0.17", {"start": v(38.1, 142.88) * mm, "end": v(44.45, 142.88) * mm});
            skLineSegment(sketch, "E118.2.0.18", {"start": v(38.1, -56.7) * mm, "end": v(44.45, -56.7) * mm});
            skLineSegment(sketch, "E118.2.0.19", {"start": v(38.1, -82.1) * mm, "end": v(44.45, -82.1) * mm});
            skLineSegment(sketch, "E118.direction1", {"start": v(-120.65, -25.85) * mm, "end": v(-38.1, -25.85) * mm, "construction": true});
            skLineSegment(sketch, "E119.bottom", {"start": v(-97.06, -180.97) * mm, "end": v(-71.66, -180.97) * mm});
            skLineSegment(sketch, "E119.top", {"start": v(-97.06, -174.62) * mm, "end": v(-71.66, -174.62) * mm});
            skLineSegment(sketch, "E119.left", {"start": v(-97.06, -180.97) * mm, "end": v(-97.06, -174.62) * mm});
            skLineSegment(sketch, "E119.right", {"start": v(-71.66, -180.97) * mm, "end": v(-71.66, -174.62) * mm});
            skLineSegment(sketch, "E120.0.1.0", {"start": v(-71.66, -98.42) * mm, "end": v(-71.66, -92.07) * mm});
            skLineSegment(sketch, "E120.0.1.1", {"start": v(-97.06, -98.42) * mm, "end": v(-97.06, -92.07) * mm});
            skLineSegment(sketch, "E120.0.1.2", {"start": v(-97.06, -98.42) * mm, "end": v(-71.66, -98.42) * mm});
            skLineSegment(sketch, "E120.0.1.3", {"start": v(-97.06, -92.07) * mm, "end": v(-71.66, -92.07) * mm});
            skLineSegment(sketch, "E120.1.0.0", {"start": v(-15.42, -180.97) * mm, "end": v(-15.42, -174.62) * mm});
            skLineSegment(sketch, "E120.1.0.1", {"start": v(-40.82, -180.97) * mm, "end": v(-40.82, -174.62) * mm});
            skLineSegment(sketch, "E120.1.0.2", {"start": v(-40.82, -180.97) * mm, "end": v(-15.42, -180.97) * mm});
            skLineSegment(sketch, "E120.1.0.3", {"start": v(-40.82, -174.62) * mm, "end": v(-15.42, -174.62) * mm});
            skLineSegment(sketch, "E120.1.1.0", {"start": v(-15.42, -98.42) * mm, "end": v(-15.42, -92.07) * mm});
            skLineSegment(sketch, "E120.1.1.1", {"start": v(-40.82, -98.42) * mm, "end": v(-40.82, -92.07) * mm});
            skLineSegment(sketch, "E120.1.1.2", {"start": v(-40.82, -98.42) * mm, "end": v(-15.42, -98.42) * mm});
            skLineSegment(sketch, "E120.1.1.3", {"start": v(-40.82, -92.07) * mm, "end": v(-15.42, -92.07) * mm});
            skLineSegment(sketch, "E120.2.0.0", {"start": v(40.82, -180.97) * mm, "end": v(40.82, -174.62) * mm});
            skLineSegment(sketch, "E120.2.0.1", {"start": v(15.42, -180.97) * mm, "end": v(15.42, -174.62) * mm});
            skLineSegment(sketch, "E120.2.0.2", {"start": v(15.42, -180.97) * mm, "end": v(40.82, -180.97) * mm});
            skLineSegment(sketch, "E120.2.0.3", {"start": v(15.42, -174.62) * mm, "end": v(40.82, -174.62) * mm});
            skLineSegment(sketch, "E120.2.1.0", {"start": v(40.82, -98.42) * mm, "end": v(40.82, -92.07) * mm});
            skLineSegment(sketch, "E120.2.1.1", {"start": v(15.42, -98.42) * mm, "end": v(15.42, -92.07) * mm});
            skLineSegment(sketch, "E120.2.1.2", {"start": v(15.42, -98.42) * mm, "end": v(40.82, -98.42) * mm});
            skLineSegment(sketch, "E120.2.1.3", {"start": v(15.42, -92.07) * mm, "end": v(40.82, -92.07) * mm});
            skLineSegment(sketch, "E120.3.0.0", {"start": v(97.06, -180.97) * mm, "end": v(97.06, -174.62) * mm});
            skLineSegment(sketch, "E120.3.0.1", {"start": v(71.66, -180.97) * mm, "end": v(71.66, -174.62) * mm});
            skLineSegment(sketch, "E120.3.0.2", {"start": v(71.66, -180.97) * mm, "end": v(97.06, -180.97) * mm});
            skLineSegment(sketch, "E120.3.0.3", {"start": v(71.66, -174.62) * mm, "end": v(97.06, -174.62) * mm});
            skLineSegment(sketch, "E120.3.1.0", {"start": v(97.06, -98.42) * mm, "end": v(97.06, -92.07) * mm});
            skLineSegment(sketch, "E120.3.1.1", {"start": v(71.66, -98.42) * mm, "end": v(71.66, -92.07) * mm});
            skLineSegment(sketch, "E120.3.1.2", {"start": v(71.66, -98.42) * mm, "end": v(97.06, -98.42) * mm});
            skLineSegment(sketch, "E120.3.1.3", {"start": v(71.66, -92.07) * mm, "end": v(97.06, -92.07) * mm});
            skLineSegment(sketch, "E120.direction1", {"start": v(-71.66, -180.97) * mm, "end": v(-15.42, -180.97) * mm, "construction": true});
            skLineSegment(sketch, "E120.direction2", {"start": v(-71.66, -180.97) * mm, "end": v(-71.66, -98.42) * mm, "construction": true});
            skSolve(sketch);
        }
        {
            var Q0;
            Q0 = qSketchRegion(id + "F6", true);
            extrude(context, id + "F7", {"entities" : qUnion([Q0]), "operationType" : NewBodyOperationType.REMOVE, "endBound" : BoundingType.THROUGH_ALL, "oppositeDirection" : true, "depth" : 25.4 * mm});
        }
    });
